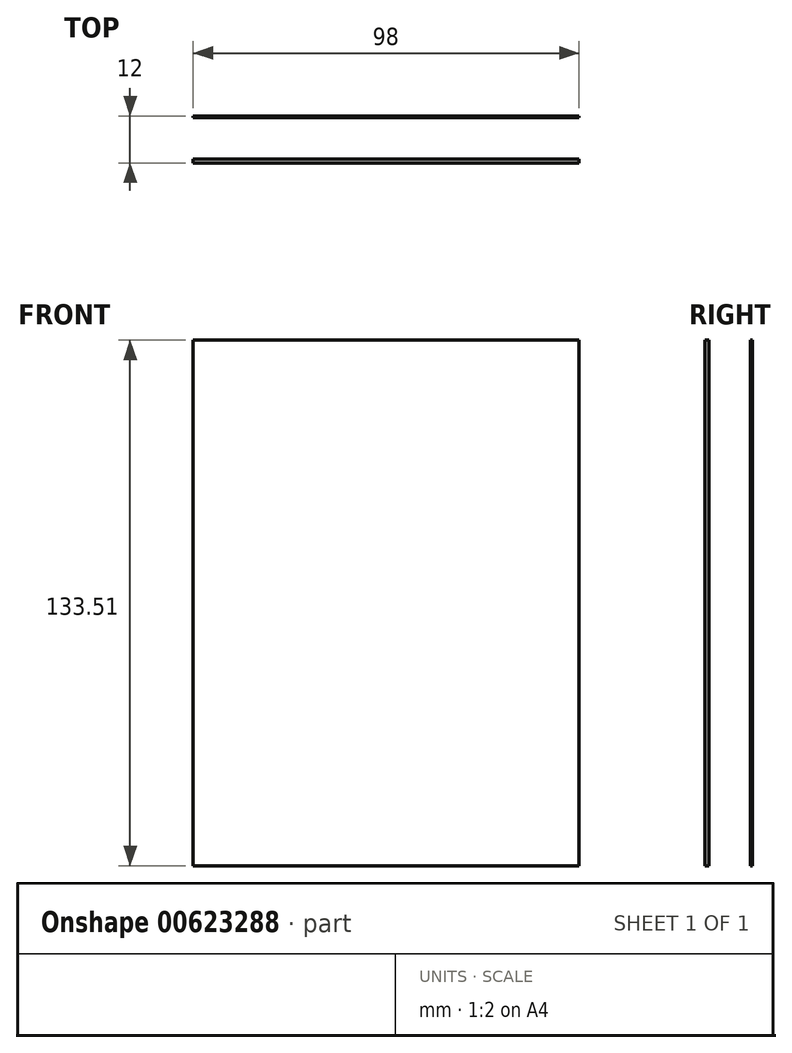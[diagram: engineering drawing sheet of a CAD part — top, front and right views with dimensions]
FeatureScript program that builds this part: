
annotation { "Feature Type Name" : "Feature", "Feature Type Description" : "" }
export const myFeature = defineFeature(function(context is Context, id is Id, definition is map)
    precondition{}
    {
        {
            var Q0;
            Q0=qCreatedBy(makeId("Front.planeOp"),FACE);
            var sketch = newSketch(context, id + "F0", { "sketchPlane" : qUnion([Q0])});
            skLineSegment(sketch, "E0.bottom", {"start": v(0, 0) * mm, "end": v(-98, 0) * mm});
            skLineSegment(sketch, "E0.top", {"start": v(0, 133.51) * mm, "end": v(-98, 133.51) * mm});
            skLineSegment(sketch, "E0.left", {"start": v(0, 0) * mm, "end": v(0, 133.51) * mm});
            skLineSegment(sketch, "E0.right", {"start": v(-98, 0) * mm, "end": v(-98, 133.51) * mm});
            skSolve(sketch);
        }
        {
            var Q0;
            Q0=makeQuery(id+"F0.imprint","IMPRINT",FACE,{"disambiguationData":[TD([[makeQuery(id+"F0.imprint","IMPRINT",EDGE,{"derivedFrom":sQuery(id+"F0.wireOp",EDGE,"E0.bottom")}),-1.0]])]});
            extrude(context, id + "F1", {"entities" : qUnion([Q0]), "depth" : 0.5 * mm, "offsetDistance" : 25 * mm});
        }
        {
            var Q0;
            Q0=qCreatedBy(makeId("Front.planeOp"),FACE);
            var sketch = newSketch(context, id + "F2", { "sketchPlane" : qUnion([Q0])});
            skLineSegment(sketch, "E1.0", {"start": v(0, 0) * mm, "end": v(-98, 0) * mm});
            skLineSegment(sketch, "E1.1", {"start": v(0, 133.51) * mm, "end": v(-98, 133.51) * mm});
            skLineSegment(sketch, "E1.2", {"start": v(0, 0) * mm, "end": v(0, 133.51) * mm});
            skLineSegment(sketch, "E1.3", {"start": v(-98, 0) * mm, "end": v(-98, 133.51) * mm});
            skSolve(sketch);
        }
        {
            var Q0;
            Q0 = qSketchRegion(id + "F2", true);
            extrude(context, id + "F3", {"entities" : qUnion([Q0]), "depth" : 12 * mm, "offsetDistance" : 25 * mm, "hasSecondDirection" : true, "secondDirectionOppositeDirection" : true, "secondDirectionDepth" : -11 * mm});
        }
    });
